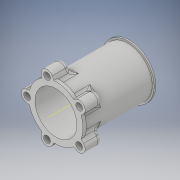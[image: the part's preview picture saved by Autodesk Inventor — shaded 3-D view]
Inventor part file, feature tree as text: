
AUTODESK INVENTOR PART (.ipt)
format: ipt  version: 2018 (Build 220112000, 112)  size: 410,112 bytes
history: native  units: in
note: dims shown in document units (in); Inventor stores cm internally (conversion verified against a paired STEP export)
features: sketch x7, extrude x6, fillet x2, pattern_circular x2, other x1
ambient origin geometry x8: Origin, YZ Plane, XZ Plane, XY Plane, X Axis, Y Axis, Z Axis, Center Point
bodies: Solid1 (feature_tree)
feature tree (18):
  extrude  "Extrusion1"  Depth=5.6693in
  extrude  "Extrusion2"  Depth=6.2992in
  extrude  "Extrusion3"  Depth=6.1024in
  sketch  "Sketch6"  dims[d8=0.1969in d9=0.0in d11=0.2474in]
  extrude  "Extrusion4"  Depth=0.2474in
  extrude  "Extrusion5"  Depth=1.378in
  fillet  "Fillet1"  Radius=3.3465in
  fillet  "Fillet2"  Radius=1.9685in
  other  "Work Axis1"
  pattern_circular  "Circular Pattern1"  [2 undecoded]
  extrude  "Extrusion6"  Depth=1.9685in TaperAngle=360.0deg
  pattern_circular  "Circular Pattern2"  Count=4  [1 undecoded]
  sketch  "Sketch9"  dims[d20=0.4724in d21=0.4724in d22=1.9685in d23=360.0deg d25=1.5748in d26=0.0in d27=1.9685in d28=360.0deg]
  sketch  "Sketch1"  dims[d0=4.8819in d1=5.6693in]
  sketch  "Sketch2"  dims[d2=8.563in d3=0.0in d4=6.2992in]
  sketch  "Sketch3"  dims[d5=0.3937in d6=0.0in d7=6.1024in]
  sketch  "Sketch7"  dims[d12=0.7874in d13=1.378in d14=3.3465in d15=1.9685in d16=0.0in]
  sketch  "Sketch8"  dims[d17=0.1969in d18=0.0in]
note: 3 required parameter values undecoded (feature->parameter linkage not recoverable at this tier; creation-order binding heuristic only, values carry confidence <= 0.55)
